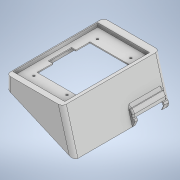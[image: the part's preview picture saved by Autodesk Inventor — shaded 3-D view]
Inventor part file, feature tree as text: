
AUTODESK INVENTOR PART (.ipt)
format: ipt  version: 2022 (Build 260153000, 153)  size: 789,504 bytes
history: native  units: mm
features: extrude x28, sketch x24, projected_geometry x10, sweep x4, fillet x2, plane x1, chamfer x1
ambient origin geometry x8: Origin, YZ Plane, XZ Plane, XY Plane, X Axis, Y Axis, Z Axis, Center Point
bodies: Solid1 (feature_tree)
feature tree (70):
  extrude  "Extrusion1"  Depth=193.2mm
  extrude  "Extrusion2"  Depth=4.2mm
  extrude  "Extrusion3"  Depth=65.697mm
  extrude  "Extrusion4"  Depth=4.2mm
  extrude  "Extrusion5"  Depth=126.501mm
  extrude  "Extrusion6"  Depth=22.6mm
  extrude  "Extrusion7"  Depth=8.0mm
  sweep  "Sweep1"
  plane  "Work Plane1"
  extrude  "Extrusion8"  Depth=11.0mm
  sweep  "Sweep2"
  sketch  "Sketch14"  dims[d10=0.0mm d11=22.6mm]
  extrude  "Extrusion9"  Depth=79.0mm
  sweep  "Sweep4"
  extrude  "Extrusion10"  Depth=40.0mm
  extrude  "Extrusion11"  Depth=9.0mm TaperAngle=0.0deg
  chamfer  "Chamfer1"  Distance=72.0mm
  extrude  "Extrusion12"  Depth=4.083461mm
  extrude  "Extrusion13"  Depth=1000.0mm TaperAngle=0.0deg
  sweep  "Sweep5"
  extrude  "Extrusion14"  Depth=6.0mm
  extrude  "Extrusion15"  Depth=8.0mm
  extrude  "Extrusion24"  TaperAngle=0.0deg  [1 undecoded]
  extrude  "Extrusion25"  TaperAngle=90.0deg  [1 undecoded]
  extrude  "Extrusion26"  Depth=2.0mm
  fillet  "Fillet1"  Radius=1000.0mm
  extrude  "Extrusion27"  Depth=10.0mm
  extrude  "Extrusion28"  Depth=8.0mm
  fillet  "Fillet2"  Radius=8.0mm
  extrude  "Extrusion29"  Depth=10.0mm
  extrude  "Extrusion30"  Depth=17.0mm
  extrude  "Extrusion31"  Depth=8.0mm
  extrude  "Extrusion32"  Depth=8.0mm
  extrude  "Extrusion33"  Depth=17.0mm
  extrude  "Extrusion34"  TaperAngle=0.0deg  [1 undecoded]
  extrude  "Extrusion35"  Depth=10.0mm
  extrude  "Extrusion36"  Depth=8.0mm
  sketch  "Sketch1"  dims[d0=110.94mm d1=193.2mm]
  sketch  "Sketch2"  dims[d2=4.2mm d3=4.2mm]
  projected_geometry  "Projected Loop1"
  sketch  "Sketch5"  dims[d4=65.7mm d5=65.697mm]
  projected_geometry  "Projected Loop2"
  projected_geometry  "Projected Loop3"
  sketch  "Sketch8"  dims[d6=4.2mm d7=4.2mm]
  sketch  "3D Sketch1"
  sketch  "Sketch11"  dims[d8=126.2mm d9=126.501mm]
  projected_geometry  "Projected Loop5"
  projected_geometry  "Projected Loop6"
  sketch  "3D Sketch2"
  projected_geometry  "Projected Loop7"
  projected_geometry  "Projected Loop8"
  sketch  "3D Sketch4"
  sketch  "Sketch18"  dims[d12=35.0mm d13=8.0mm]
  sketch  "Sketch23"  dims[d14=2.0mm d15=0.0mm d16=2.0mm]
  sketch  "Sketch24"  dims[d17=14.0mm d18=11.0mm]
  projected_geometry  "Projected Loop11"
  sketch  "3D Sketch5"
  sketch  "Sketch31"  dims[d19=6.0mm d20=7.5mm d21=0.0mm]
  projected_geometry  "Projected Loop14"
  sketch  "Sketch48"  dims[d22=105.0mm d23=79.0mm]
  projected_geometry  "Projected Loop15"
  sketch  "Sketch51"  dims[d24=6.0mm d25=30.0mm]
  sketch  "Sketch52"  dims[d26=40.0mm d27=40.0mm]
  sketch  "Sketch53"  dims[d28=9.0mm d29=7.5mm d30=0.0mm]
  sketch  "Sketch57"  dims[d39=2.0mm d40=72.0mm d41=0.0mm]
  sketch  "Sketch58"  dims[d42=23.5mm d47=4.083461mm]
  sketch  "Sketch60"  dims[d48=140.0mm d49=1000.0mm d50=0.0mm]
  sketch  "Sketch61"  dims[d51=23.1125mm d52=23.113mm]
  sketch  "Sketch62"  dims[d53=63.0mm d54=0.0mm d55=6.0mm]
  sketch  "Sketch63"  dims[d56=1000.0mm d57=0.0mm d58=8.0mm d59=0.0mm d60=0.0mm d62=90.0deg d64=2.0mm d65=1000.0mm d66=0.0mm d80=13.0mm d81=8.0mm d82=8.0mm d83=13.0mm d84=17.0mm d85=8.0mm d86=8.0mm d87=17.0mm d88=0.0mm d89=0.0mm d90=13.0mm d91=8.0mm d92=13.0mm d93=8.0mm d96=10.0mm d97=0.0mm d98=0.0mm d99=0.0mm d100=1000.0mm d101=0.0mm d102=4.2mm d103=5.5mm d104=13.0mm d105=4.2mm d106=4.2mm d107=4.2mm d108=10.0mm d109=5.5mm d110=5.5mm d111=10.0mm d112=13.0mm d113=5.5mm d114=9.0mm d115=0.0mm d116=0.8mm d117=2.0mm d118=45.0deg d121=9.0mm d122=0.0mm d123=10.0mm d124=0.0mm d127=2.0mm d128=0.0mm d129=0.0mm d130=1000.0mm d131=0.0mm d133=71.586mm d134=67.15mm d135=0.0mm d136=0.0mm d137=16.0mm d138=0.0mm d175=14.17mm d176=3.0mm d178=5.0mm d179=20.100957mm d180=10.0mm d183=2.0mm d184=20.100957mm d185=3.2mm d187=2.0mm d188=8.0mm d189=10.0mm d190=0.0mm d191=2.0mm d192=0.0mm d193=2.0mm d194=0.0mm d195=3.0mm d196=2.0mm d197=0.0mm d198=9.0mm d199=5.65mm d200=10.0mm d201=0.0mm d202=3.0mm d203=9.0mm d204=8.5mm d205=1.5mm d206=0.0mm d207=5.8mm d208=13.4mm d209=16.0mm d210=1.5mm d211=1.3mm d212=1.5mm d213=0.0mm d216=0.0mm d217=7.4mm d218=2.3mm d222=135.0deg d223=135.0deg d224=1.314871mm d225=1.314871mm d226=8.0mm d227=19.049mm d228=3.3mm d229=10.0mm d230=0.0mm d231=15.8mm d232=4.2mm d233=4.2mm d234=3.6mm d235=1.0mm d236=1.0mm d237=1.0mm d238=1.5mm d239=0.0mm d241=22.597mm d242=10.0mm d243=0.0mm d244=1000.0mm d245=0.0mm d246=10.0mm d247=0.0mm d250=0.5mm d251=0.5mm d252=10.0mm d253=0.0mm]
note: 3 required parameter values undecoded (feature->parameter linkage not recoverable at this tier; creation-order binding heuristic only, values carry confidence <= 0.55)
